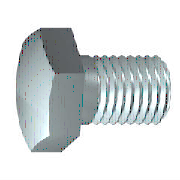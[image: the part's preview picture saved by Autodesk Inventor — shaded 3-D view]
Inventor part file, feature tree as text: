
AUTODESK INVENTOR PART (.ipt)
format: ipt  version: 2015 (Build 190159000, 159)  size: 188,928 bytes
history: native  units: mm (DEFAULTED — no unit token found)
features: other x4, plane x3, sketch x2
ambient origin geometry x6: Origin, XY Plane, X Axis, Y Axis, Z Axis, Center Point
bodies: Body1 (feature_tree)
feature tree (9):
  plane  "WorkPlane1"
  other  "WorkPoint1"
  other  "MSC_A1"
  other  "MSC_PF1"
  other  "MSC_PT1"
  plane  "WorkPlane2"
  plane  "WorkPlane3"
  sketch  "Szkic3"
  sketch  "Szkic4"
